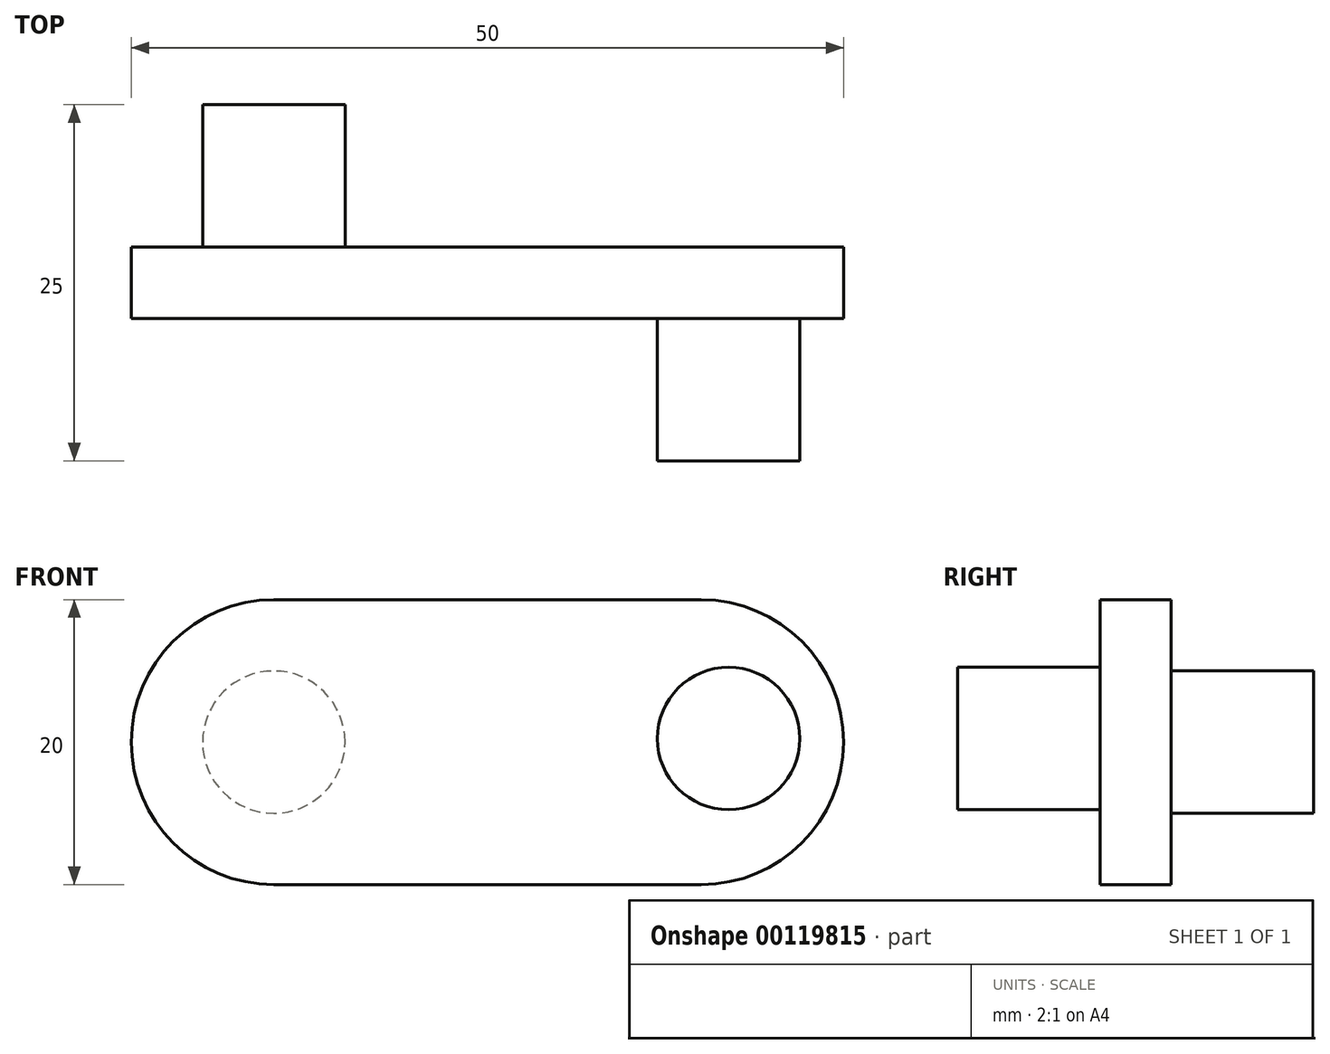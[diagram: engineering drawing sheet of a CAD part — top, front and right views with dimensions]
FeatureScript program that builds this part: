
annotation { "Feature Type Name" : "Feature", "Feature Type Description" : "" }
export const myFeature = defineFeature(function(context is Context, id is Id, definition is map)
    precondition{}
    {
        {
            var Q0;
            Q0=qCreatedBy(makeId("Front.planeOp"),FACE);
            var sketch = newSketch(context, id + "F0", { "sketchPlane" : qUnion([Q0])});
            skArc(sketch, "E0", {"start": v(0, 20) * mm, "mid": v(-10, 10) * mm, "end": v(0, 0) * mm});
            skArc(sketch, "E1", {"start": v(30, 0) * mm, "mid": v(40, 10) * mm, "end": v(30, 20) * mm});
            skLineSegment(sketch, "E2", {"start": v(0, 20) * mm, "end": v(30, 20) * mm});
            skLineSegment(sketch, "E3", {"start": v(0, 0) * mm, "end": v(30, 0) * mm});
            skCircle(sketch, "E4", {"center": v(0, 10) * mm, "radius": 5 * mm});
            skCircle(sketch, "E5", {"center": v(30, 10) * mm, "radius": 5 * mm});
            skLineSegment(sketch, "E6", {"start": v(30.05, 25.52) * mm, "end": v(30.05, -4.2) * mm, "construction": true});
            skLineSegment(sketch, "E7", {"start": v(0, 22.77) * mm, "end": v(0, -5.86) * mm, "construction": true});
            skLineSegment(sketch, "E8", {"start": v(-12.26, 10) * mm, "end": v(44.21, 10) * mm, "construction": true});
            skPoint(sketch, "E8.startSnap0", {"position": v(-10, 10) * mm});
            skSolve(sketch);
        }
        {
            var Q0;
            Q0 = qSketchRegion(id + "F0", true);
            var Q1;
            Q1=makeQuery(id+"F0.imprint","IMPRINT",FACE,{"disambiguationData":[TD([[makeQuery(id+"F0.imprint","IMPRINT",EDGE,{"derivedFrom":sQuery(id+"F0.wireOp",EDGE,"E4")}),1.0]])]});
            var Q2;
            Q2=makeQuery(id+"F0.imprint","IMPRINT",FACE,{"disambiguationData":[TD([[makeQuery(id+"F0.imprint","IMPRINT",EDGE,{"derivedFrom":sQuery(id+"F0.wireOp",EDGE,"E5")}),1.0]])]});
            extrude(context, id + "F1", {"entities" : qUnion([Q0, Q1, Q2]), "depth" : 5 * mm});
        }
        {
            var Q0;
            Q0=makeQuery(id+"F1.opExtrude","CAP_FACE",FACE,{"disambiguationData":[OSD([sQuery(id+"F0.wireOp",EDGE,"E0"),sQuery(id+"F0.wireOp",EDGE,"E1"),sQuery(id+"F0.wireOp",EDGE,"E2"),sQuery(id+"F0.wireOp",EDGE,"E3")])],"isStart":true});
            var sketch = newSketch(context, id + "F2", { "sketchPlane" : qUnion([Q0])});
            skCircle(sketch, "E9", {"center": v(0, 10) * mm, "radius": 5 * mm});
            skSolve(sketch);
        }
        {
            var Q0;
            Q0=makeQuery(id+"F2.imprint","IMPRINT",FACE,{"disambiguationData":[TD([[makeQuery(id+"F2.imprint","IMPRINT",EDGE,{"derivedFrom":sQuery(id+"F2.wireOp",EDGE,"E9")}),1.0]])]});
            extrude(context, id + "F3", {"entities" : qUnion([Q0]), "operationType" : NewBodyOperationType.ADD, "depth" : 10 * mm});
        }
        {
            var Q0;
            Q0=makeQuery(id+"F1.opExtrude","CAP_FACE",FACE,{"disambiguationData":[OSD([sQuery(id+"F0.wireOp",EDGE,"E0"),sQuery(id+"F0.wireOp",EDGE,"E1"),sQuery(id+"F0.wireOp",EDGE,"E2"),sQuery(id+"F0.wireOp",EDGE,"E3")])],"isStart":false});
            var sketch = newSketch(context, id + "F4", { "sketchPlane" : qUnion([Q0])});
            skCircle(sketch, "E10", {"center": v(31.93, 10.25) * mm, "radius": 5 * mm});
            skSolve(sketch);
        }
        {
            var Q0;
            Q0=makeQuery(id+"F4.imprint","IMPRINT",FACE,{"disambiguationData":[TD([[makeQuery(id+"F4.imprint","IMPRINT",EDGE,{"derivedFrom":sQuery(id+"F4.wireOp",EDGE,"E10")}),1.0]])]});
            extrude(context, id + "F5", {"entities" : qUnion([Q0]), "operationType" : NewBodyOperationType.ADD, "depth" : 10 * mm});
        }
    });
